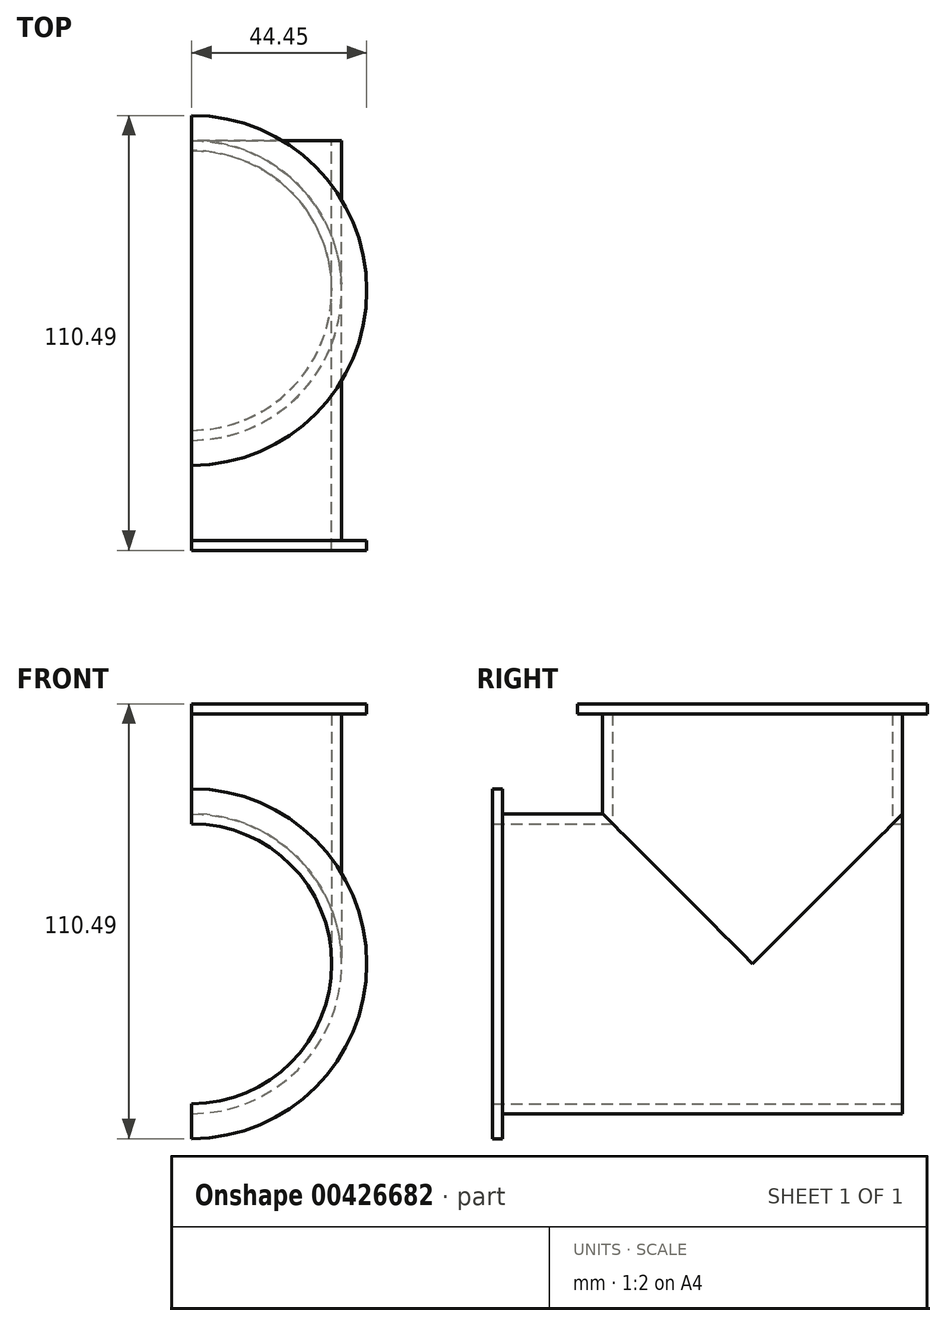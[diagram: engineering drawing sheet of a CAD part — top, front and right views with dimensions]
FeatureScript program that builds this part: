
annotation { "Feature Type Name" : "Feature", "Feature Type Description" : "" }
export const myFeature = defineFeature(function(context is Context, id is Id, definition is map)
    precondition{}
    {
        {
            var Q0;
            Q0=qCreatedBy(makeId("Front.planeOp"),FACE);
            var sketch = newSketch(context, id + "F0", { "sketchPlane" : qUnion([Q0])});
            skArc(sketch, "E0", {"start": v(0, -38.1) * mm, "mid": v(38.1, 0) * mm, "end": v(0, 38.1) * mm});
            skLineSegment(sketch, "E1", {"start": v(0, 38.1) * mm, "end": v(0, -38.1) * mm});
            skSolve(sketch);
        }
        {
            var Q0;
            Q0 = qSketchRegion(id + "F0", true);
            extrude(context, id + "F1", {"entities" : qUnion([Q0]), "depth" : 63.5 * mm});
        }
        {
            var Q0;
            Q0=qCreatedBy(makeId("Top.planeOp"),FACE);
            var sketch = newSketch(context, id + "F2", { "sketchPlane" : qUnion([Q0])});
            skArc(sketch, "E2", {"start": v(0, -38.1) * mm, "mid": v(38.1, 0) * mm, "end": v(0, 38.1) * mm});
            skLineSegment(sketch, "E3", {"start": v(0, 38.1) * mm, "end": v(0, -38.1) * mm});
            skSolve(sketch);
        }
        {
            var Q0;
            Q0=makeQuery(id+"F2.imprint","IMPRINT",FACE,{"disambiguationData":[TD([[makeQuery(id+"F2.imprint","IMPRINT",EDGE,{"derivedFrom":sQuery(id+"F2.wireOp",EDGE,"E2")}),1.0]])]});
            extrude(context, id + "F3", {"entities" : qUnion([Q0]), "operationType" : NewBodyOperationType.ADD, "depth" : 63.5 * mm});
        }
        {
            var Q0;
            Q0=makeQuery(id+"F0.imprint","IMPRINT",FACE,{"disambiguationData":[TD([[makeQuery(id+"F0.imprint","IMPRINT",EDGE,{"derivedFrom":sQuery(id+"F0.wireOp",EDGE,"E0")}),1.0]])]});
            var Q1;
            Q1 = qSketchRegion(id + "F0", true);
            extrude(context, id + "F4", {"entities" : qUnion([Q0, Q1]), "operationType" : NewBodyOperationType.ADD, "depth" : 76.2 * mm, "symmetric" : true});
        }
        {
            var Q0;
            Q0=makeQuery(id+"F3.opExtrude","CAP_FACE",FACE,{"disambiguationData":[OSD([sQuery(id+"F2.wireOp",EDGE,"E2"),sQuery(id+"F2.wireOp",EDGE,"E3")])],"isStart":false});
            var sketch = newSketch(context, id + "F5", { "sketchPlane" : qUnion([Q0])});
            skArc(sketch, "E4.0", {"start": v(0, -44.45) * mm, "mid": v(44.45, 0) * mm, "end": v(0, 44.45) * mm});
            skLineSegment(sketch, "E5", {"start": v(0, -44.45) * mm, "end": v(0, 44.45) * mm});
            skSolve(sketch);
        }
        {
            var Q0;
            Q0 = qSketchRegion(id + "F5", true);
            extrude(context, id + "F6", {"entities" : qUnion([Q0]), "operationType" : NewBodyOperationType.ADD, "depth" : 2.54 * mm});
        }
        {
            var Q0;
            Q0=makeQuery(id+"F1.opExtrude","CAP_FACE",FACE,{"disambiguationData":[OSD([sQuery(id+"F0.wireOp",EDGE,"E0"),sQuery(id+"F0.wireOp",EDGE,"E1")])],"isStart":false});
            var sketch = newSketch(context, id + "F7", { "sketchPlane" : qUnion([Q0])});
            skArc(sketch, "E6.0", {"start": v(0, -44.45) * mm, "mid": v(44.45, 0) * mm, "end": v(0, 44.45) * mm});
            skLineSegment(sketch, "E7", {"start": v(0, 44.45) * mm, "end": v(0, 35.56) * mm});
            skArc(sketch, "E8.0", {"start": v(0, -35.56) * mm, "mid": v(35.56, 0) * mm, "end": v(0, 35.56) * mm});
            skLineSegment(sketch, "E9.trimOffspring", {"start": v(0, -35.56) * mm, "end": v(0, -44.45) * mm});
            skSolve(sketch);
        }
        {
            var Q0;
            {var subQ0=sQuery(id+"F7.wireOp",EDGE,"E6.0");Q0=makeQuery(id+"F7.imprint","IMPRINT",FACE,{"disambiguationData":[TD([[makeQuery(id+"F7.imprint","IMPRINT",EDGE,{"derivedFrom":subQ0}),1.0]])]});}
            var Q1;
            {var subQ1=makeQuery(id+"F1.opExtrude","CAP_EDGE",EDGE,{"disambiguationData":[OSD([sQuery(id+"F0.wireOp",EDGE,"E0")])],"isStart":false});Q1=makeQuery(id+"F7.imprint","IMPRINT",FACE,{"disambiguationData":[TD([[makeQuery(id+"F7.imprint","IMPRINT",EDGE,{"derivedFrom":subQ1}),1.0]])]});}
            extrude(context, id + "F8", {"entities" : qUnion([Q0, Q1]), "operationType" : NewBodyOperationType.ADD, "depth" : 2.54 * mm});
        }
        {
            var Q0;
            {var subQ0=sQuery(id+"F0.wireOp",EDGE,"E1");Q0=makeQuery(id+"F4.boolean.opBoolean","MERGE",FACE,{"derivedFrom":[makeQuery(id+"F3.boolean.opBoolean","MERGE",FACE,{"derivedFrom":[makeQuery(id+"F1.opExtrude","SWEPT_FACE",FACE,{"disambiguationData":[OSD([subQ0])]}),makeQuery(id+"F3.opExtrude","SWEPT_FACE",FACE,{"disambiguationData":[OSD([sQuery(id+"F2.wireOp",EDGE,"E3")])]})]}),makeQuery(id+"F4.opExtrude","SWEPT_FACE",FACE,{"disambiguationData":[OSD([subQ0])]})]});}
            var Q1;
            Q1=makeQuery(id+"F1.opExtrude","CAP_FACE",FACE,{"disambiguationData":[OSD([sQuery(id+"F0.wireOp",EDGE,"E0"),sQuery(id+"F0.wireOp",EDGE,"E1")])],"isStart":false});
            var Q2;
            Q2=makeQuery(id+"F3.opExtrude","CAP_FACE",FACE,{"disambiguationData":[OSD([sQuery(id+"F2.wireOp",EDGE,"E2"),sQuery(id+"F2.wireOp",EDGE,"E3")])],"isStart":false});
            var Q3;
            Q3=makeQuery(id+"F4.opExtrude","CAP_FACE",FACE,{"disambiguationData":[OSD([sQuery(id+"F0.wireOp",EDGE,"E0"),sQuery(id+"F0.wireOp",EDGE,"E1")])],"isStart":true});
            shell(context, id + "F9", {"entities" : qUnion([Q0, Q1, Q2, Q3]), "thickness" : 2.54 * mm});
        }
    });
